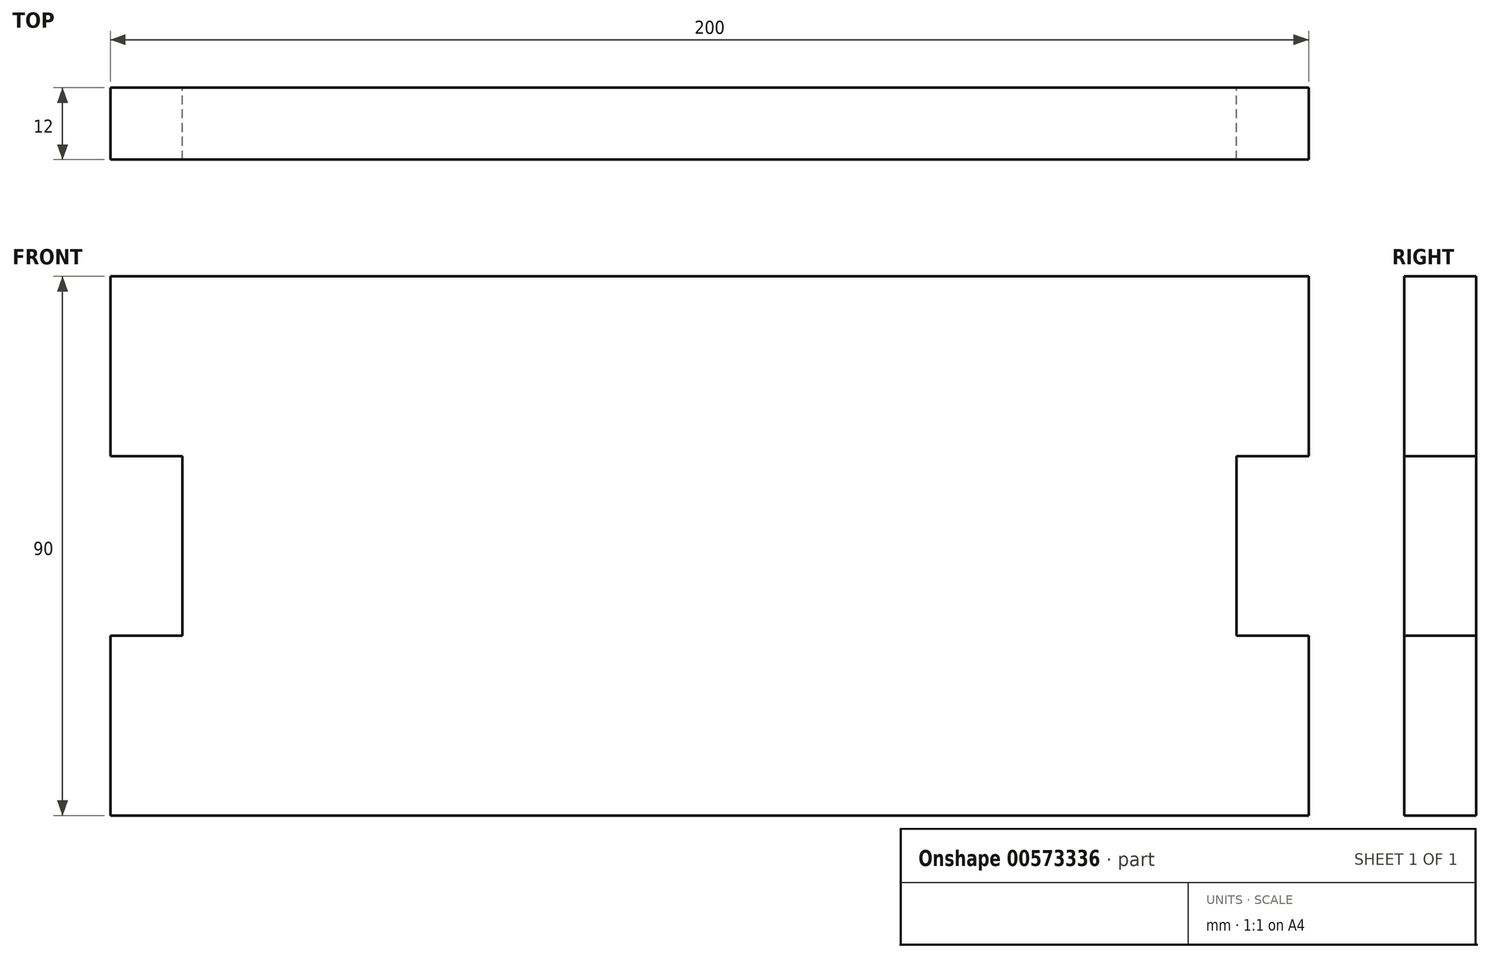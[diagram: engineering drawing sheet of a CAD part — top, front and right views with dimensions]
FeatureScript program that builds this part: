
annotation { "Feature Type Name" : "Feature", "Feature Type Description" : "" }
export const myFeature = defineFeature(function(context is Context, id is Id, definition is map)
    precondition{}
    {
        {
            var Q0;
            Q0=qCreatedBy(makeId("Front.planeOp"),FACE);
            var sketch = newSketch(context, id + "F0", { "sketchPlane" : qUnion([Q0])});
            skLineSegment(sketch, "E0", {"start": v(0, 0) * mm, "end": v(0, 30) * mm});
            skLineSegment(sketch, "E1", {"start": v(0, 30) * mm, "end": v(12, 30) * mm});
            skLineSegment(sketch, "E2", {"start": v(12, 30) * mm, "end": v(12, 60) * mm});
            skLineSegment(sketch, "E3", {"start": v(12, 60) * mm, "end": v(0, 60) * mm});
            skLineSegment(sketch, "E4", {"start": v(0, 60) * mm, "end": v(0, 90) * mm});
            skLineSegment(sketch, "E5", {"start": v(0, 90) * mm, "end": v(100, 90) * mm});
            skLineSegment(sketch, "E6", {"start": v(100, 90) * mm, "end": v(100, 0) * mm, "construction": true});
            skLineSegment(sketch, "E7", {"start": v(100, 0) * mm, "end": v(0, 0) * mm});
            skLineSegment(sketch, "E8.MirrorCS", {"start": v(200, 60) * mm, "end": v(200, 90) * mm});
            skLineSegment(sketch, "E9.MirrorCS", {"start": v(188, 60) * mm, "end": v(200, 60) * mm});
            skLineSegment(sketch, "E10.MirrorCS", {"start": v(188, 30) * mm, "end": v(188, 60) * mm});
            skLineSegment(sketch, "E11.MirrorCS", {"start": v(200, 90) * mm, "end": v(100, 90) * mm});
            skLineSegment(sketch, "E12.MirrorCS", {"start": v(100, 0) * mm, "end": v(200, 0) * mm});
            skLineSegment(sketch, "E13.MirrorCS", {"start": v(200, 30) * mm, "end": v(188, 30) * mm});
            skLineSegment(sketch, "E14.MirrorCS", {"start": v(200, 0) * mm, "end": v(200, 30) * mm});
            skSolve(sketch);
        }
        {
            var Q0;
            Q0=makeQuery(id+"F0.imprint","IMPRINT",FACE,{"disambiguationData":[TD([[makeQuery(id+"F0.imprint","IMPRINT",EDGE,{"derivedFrom":sQuery(id+"F0.wireOp",EDGE,"E0")}),-1.0]])]});
            extrude(context, id + "F1", {"entities" : qUnion([Q0]), "endBound" : BoundingType.SYMMETRIC, "depth" : 12 * mm, "offsetDistance" : 25 * mm});
        }
    });
